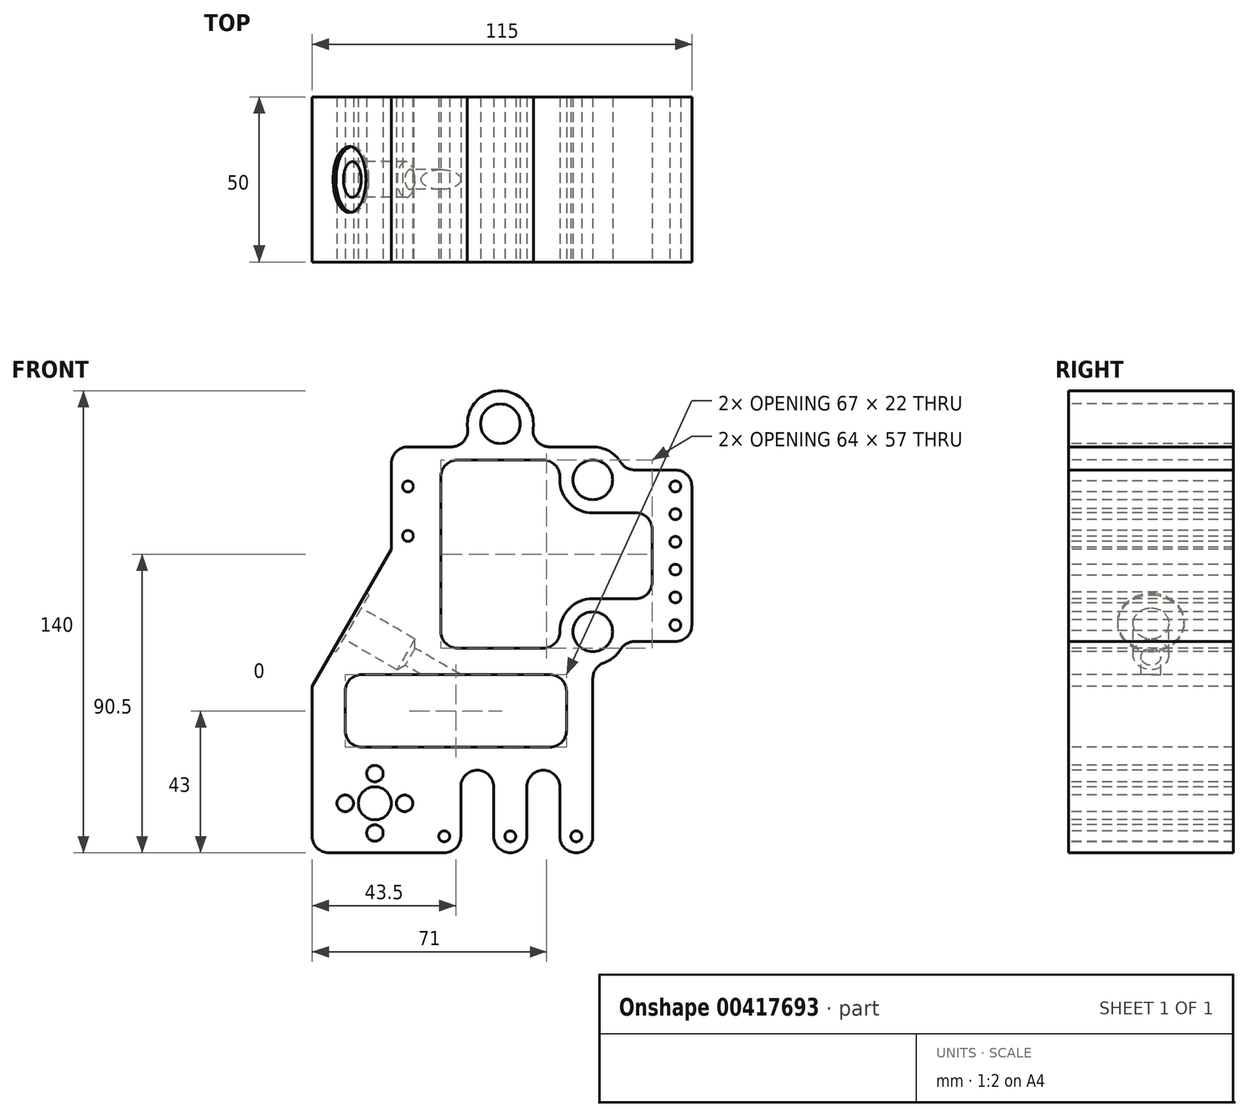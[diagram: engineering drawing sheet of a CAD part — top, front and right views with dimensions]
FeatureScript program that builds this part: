
annotation { "Feature Type Name" : "Feature", "Feature Type Description" : "" }
export const myFeature = defineFeature(function(context is Context, id is Id, definition is map)
    precondition{}
    {
        {
            var Q0;
            Q0=qCreatedBy(makeId("Front.planeOp"),FACE);
            var sketch = newSketch(context, id + "F0", { "sketchPlane" : qUnion([Q0])});
            skCircle(sketch, "E0", {"center": v(0, 50) * mm, "radius": 6 * mm});
            skCircle(sketch, "E1", {"center": v(28, 33) * mm, "radius": 6 * mm});
            skCircle(sketch, "E2", {"center": v(28, -13) * mm, "radius": 6 * mm});
            skLineSegment(sketch, "E3", {"start": v(0, 60.48) * mm, "end": v(0, 39.82) * mm, "construction": true});
            skLineSegment(sketch, "E4", {"start": v(-57, 50) * mm, "end": v(58, 50) * mm, "construction": true});
            skLineSegment(sketch, "E5", {"start": v(15.65, 33) * mm, "end": v(59.52, 33) * mm, "construction": true});
            skLineSegment(sketch, "E6", {"start": v(28, 45.63) * mm, "end": v(28, -22.58) * mm, "construction": true});
            skLineSegment(sketch, "E7", {"start": v(14.55, -13) * mm, "end": v(60.8, -13) * mm, "construction": true});
            skCircle(sketch, "E8", {"center": v(-28, 31) * mm, "radius": 2 * mm, "construction": true});
            skCircle(sketch, "E9", {"center": v(53, 31) * mm, "radius": 2 * mm, "construction": true});
            skCircle(sketch, "E10", {"center": v(23, -75) * mm, "radius": 2 * mm, "construction": true});
            skCircle(sketch, "E11", {"center": v(-38, -65) * mm, "radius": 5 * mm});
            skCircle(sketch, "E12", {"center": v(-38, -56) * mm, "radius": 3 * mm, "construction": true});
            skCircle(sketch, "E13.0.1.0", {"center": v(53, 22.6) * mm, "radius": 2 * mm, "construction": true});
            skCircle(sketch, "E13.0.2.0", {"center": v(53, 14.2) * mm, "radius": 2 * mm, "construction": true});
            skCircle(sketch, "E13.0.3.0", {"center": v(53, 5.8) * mm, "radius": 2 * mm, "construction": true});
            skCircle(sketch, "E13.0.4.0", {"center": v(53, -2.6) * mm, "radius": 2 * mm, "construction": true});
            skCircle(sketch, "E13.0.5.0", {"center": v(53, -11) * mm, "radius": 2 * mm, "construction": true});
            skLineSegment(sketch, "E13.direction1", {"start": v(53, 31) * mm, "end": v(78.37, 31) * mm, "construction": true});
            skLineSegment(sketch, "E13.direction2", {"start": v(53, 31) * mm, "end": v(53, 22.6) * mm, "construction": true});
            skCircle(sketch, "E14.0.1.0", {"center": v(-28, 16) * mm, "radius": 2 * mm, "construction": true});
            skLineSegment(sketch, "E14.direction1", {"start": v(-28, 31) * mm, "end": v(-13.33, 31) * mm, "construction": true});
            skLineSegment(sketch, "E14.direction2", {"start": v(-28, 31) * mm, "end": v(-28, 16) * mm, "construction": true});
            skCircle(sketch, "E15.1.0.0", {"center": v(3, -75) * mm, "radius": 2 * mm, "construction": true});
            skCircle(sketch, "E15.2.0.0", {"center": v(-17, -75) * mm, "radius": 2 * mm, "construction": true});
            skLineSegment(sketch, "E15.direction1", {"start": v(23, -75) * mm, "end": v(3, -75) * mm, "construction": true});
            skCircle(sketch, "E16.0", {"center": v(-38, -65) * mm, "radius": 9 * mm, "construction": true});
            skCircle(sketch, "E17.1.0", {"center": v(-47, -65) * mm, "radius": 3 * mm, "construction": true});
            skCircle(sketch, "E17.2.0", {"center": v(-38, -74) * mm, "radius": 3 * mm, "construction": true});
            skCircle(sketch, "E17.3.0", {"center": v(-29, -65) * mm, "radius": 3 * mm, "construction": true});
            skLineSegment(sketch, "E18", {"start": v(-57, 50) * mm, "end": v(-57, -80) * mm, "construction": true});
            skLineSegment(sketch, "E19", {"start": v(58, 50) * mm, "end": v(58, -80) * mm, "construction": true});
            skLineSegment(sketch, "E20", {"start": v(58, -80) * mm, "end": v(-57, -80) * mm, "construction": true});
            skSolve(sketch);
        }
        {
            var Q0;
            Q0=qCreatedBy(makeId("Front.planeOp"),FACE);
            var sketch = newSketch(context, id + "F1", { "sketchPlane" : qUnion([Q0])});
            skCircle(sketch, "E21.0", {"center": v(3, -75) * mm, "radius": 5 * mm});
            skLineSegment(sketch, "E22", {"start": v(53, 36) * mm, "end": v(40.69, 36) * mm});
            skArc(sketch, "E23", {"start": v(36.46, 38.33) * mm, "mid": v(38.27, 36.62) * mm, "end": v(40.69, 36) * mm});
            skLineSegment(sketch, "E24", {"start": v(58, 31) * mm, "end": v(58, -11) * mm});
            skLineSegment(sketch, "E25", {"start": v(53, -16) * mm, "end": v(40.69, -16) * mm});
            skArc(sketch, "E26", {"start": v(40.69, -16) * mm, "mid": v(38.27, -16.62) * mm, "end": v(36.46, -18.33) * mm});
            skLineSegment(sketch, "E27", {"start": v(28, -27.14) * mm, "end": v(28, -75) * mm});
            skArc(sketch, "E28", {"start": v(31.33, -22.43) * mm, "mid": v(28.92, -24.26) * mm, "end": v(28, -27.14) * mm});
            skLineSegment(sketch, "E29", {"start": v(18, -75) * mm, "end": v(18, -60) * mm});
            skArc(sketch, "E30", {"start": v(18, -60) * mm, "mid": v(13, -55) * mm, "end": v(8, -60) * mm});
            skLineSegment(sketch, "E31", {"start": v(8, -60) * mm, "end": v(8, -75) * mm});
            skLineSegment(sketch, "E32.1.0.0", {"start": v(-12, -60) * mm, "end": v(-12, -75) * mm});
            skArc(sketch, "E32.1.0.1", {"start": v(-2, -60) * mm, "mid": v(-7, -55) * mm, "end": v(-12, -60) * mm});
            skLineSegment(sketch, "E32.1.0.2", {"start": v(-2, -75) * mm, "end": v(-2, -60) * mm});
            skLineSegment(sketch, "E32.direction1", {"start": v(8, -75) * mm, "end": v(-12, -75) * mm, "construction": true});
            skLineSegment(sketch, "E33", {"start": v(-17, -80) * mm, "end": v(-52, -80) * mm});
            skArc(sketch, "E34", {"start": v(-57, -75) * mm, "mid": v(-55.54, -78.54) * mm, "end": v(-52, -80) * mm});
            skLineSegment(sketch, "E35", {"start": v(-57, -75) * mm, "end": v(-57, -29.57) * mm});
            skLineSegment(sketch, "E36", {"start": v(-57, -29.57) * mm, "end": v(-33, 12) * mm});
            skLineSegment(sketch, "E37", {"start": v(-33, 12) * mm, "end": v(-33, 38) * mm});
            skArc(sketch, "E38", {"start": v(-28, 43) * mm, "mid": v(-31.54, 41.54) * mm, "end": v(-33, 38) * mm});
            skLineSegment(sketch, "E39", {"start": v(-28, 43) * mm, "end": v(-14.87, 43) * mm});
            skArc(sketch, "E40", {"start": v(-14.87, 43) * mm, "mid": v(-11.1, 44.7) * mm, "end": v(-9.91, 48.67) * mm});
            skLineSegment(sketch, "E41", {"start": v(28, 43) * mm, "end": v(14.87, 43) * mm});
            skArc(sketch, "E42", {"start": v(9.91, 48.67) * mm, "mid": v(11.1, 44.7) * mm, "end": v(14.87, 43) * mm});
            skArc(sketch, "E43", {"start": v(9.91, 48.67) * mm, "mid": v(0, 60) * mm, "end": v(-9.91, 48.67) * mm});
            skArc(sketch, "E44", {"start": v(-9.91, 48.67) * mm, "mid": v(0, 40) * mm, "end": v(9.91, 48.67) * mm, "construction": true});
            skArc(sketch, "E45", {"start": v(28, 43) * mm, "mid": v(23.17, 24.24) * mm, "end": v(36.46, 38.33) * mm, "construction": true});
            skArc(sketch, "E46", {"start": v(36.46, 38.33) * mm, "mid": v(32.83, 41.76) * mm, "end": v(28, 43) * mm});
            skArc(sketch, "E47", {"start": v(53, 36) * mm, "mid": v(49.46, 27.46) * mm, "end": v(58, 31) * mm, "construction": true});
            skArc(sketch, "E48", {"start": v(58, 31) * mm, "mid": v(56.54, 34.54) * mm, "end": v(53, 36) * mm});
            skArc(sketch, "E49", {"start": v(58, -11) * mm, "mid": v(49.46, -7.46) * mm, "end": v(53, -16) * mm, "construction": true});
            skArc(sketch, "E50", {"start": v(53, -16) * mm, "mid": v(56.54, -14.54) * mm, "end": v(58, -11) * mm});
            skArc(sketch, "E51", {"start": v(36.46, -18.33) * mm, "mid": v(21.76, -5.19) * mm, "end": v(31.33, -22.43) * mm, "construction": true});
            skArc(sketch, "E52", {"start": v(31.33, -22.43) * mm, "mid": v(34.24, -20.81) * mm, "end": v(36.46, -18.33) * mm});
            skArc(sketch, "E53", {"start": v(28, -75) * mm, "mid": v(23, -70) * mm, "end": v(18, -75) * mm, "construction": true});
            skArc(sketch, "E54", {"start": v(18, -75) * mm, "mid": v(23, -80) * mm, "end": v(28, -75) * mm});
            skArc(sketch, "E55", {"start": v(-12, -75) * mm, "mid": v(-20.54, -71.46) * mm, "end": v(-17, -80) * mm, "construction": true});
            skArc(sketch, "E56", {"start": v(-17, -80) * mm, "mid": v(-13.46, -78.54) * mm, "end": v(-12, -75) * mm});
            skLineSegment(sketch, "E57", {"start": v(-18, 34) * mm, "end": v(-18, -13) * mm});
            skArc(sketch, "E58", {"start": v(-18, -13) * mm, "mid": v(-16.54, -16.54) * mm, "end": v(-13, -18) * mm});
            skLineSegment(sketch, "E59", {"start": v(-13, -18) * mm, "end": v(13, -18) * mm});
            skArc(sketch, "E60", {"start": v(13, -18) * mm, "mid": v(16.54, -16.54) * mm, "end": v(18, -13) * mm});
            skArc(sketch, "E61", {"start": v(-13, 39) * mm, "mid": v(-16.54, 37.54) * mm, "end": v(-18, 34) * mm});
            skLineSegment(sketch, "E62", {"start": v(-13, 39) * mm, "end": v(13, 39) * mm});
            skArc(sketch, "E63", {"start": v(18, 33) * mm, "mid": v(20.93, 25.93) * mm, "end": v(28, 23) * mm});
            skLineSegment(sketch, "E64", {"start": v(28, 23) * mm, "end": v(41, 23) * mm});
            skArc(sketch, "E65", {"start": v(46, 18) * mm, "mid": v(44.54, 21.54) * mm, "end": v(41, 23) * mm});
            skLineSegment(sketch, "E66", {"start": v(46, 18) * mm, "end": v(46, 2) * mm});
            skArc(sketch, "E67", {"start": v(41, -3) * mm, "mid": v(44.54, -1.54) * mm, "end": v(46, 2) * mm});
            skLineSegment(sketch, "E68", {"start": v(41, -3) * mm, "end": v(28, -3) * mm});
            skLineSegment(sketch, "E69", {"start": v(18, 33) * mm, "end": v(18, 34) * mm});
            skArc(sketch, "E70", {"start": v(18, 34) * mm, "mid": v(16.54, 37.54) * mm, "end": v(13, 39) * mm});
            skLineSegment(sketch, "E71", {"start": v(18, -13) * mm, "end": v(18, -13) * mm});
            skArc(sketch, "E72", {"start": v(28, -3) * mm, "mid": v(20.93, -5.93) * mm, "end": v(18, -13) * mm});
            skLineSegment(sketch, "E73.bottom", {"start": v(-42, -26) * mm, "end": v(15, -26) * mm});
            skLineSegment(sketch, "E73.top", {"start": v(-42, -48) * mm, "end": v(15, -48) * mm});
            skLineSegment(sketch, "E73.left", {"start": v(-47, -31) * mm, "end": v(-47, -43) * mm});
            skLineSegment(sketch, "E73.right", {"start": v(20, -31) * mm, "end": v(20, -43) * mm});
            skPoint(sketch, "E74.visualSharp", {"position": v(-47, -26) * mm});
            skArc(sketch, "E74.filletArc", {"start": v(-42, -26) * mm, "mid": v(-45.54, -27.46) * mm, "end": v(-47, -31) * mm});
            skPoint(sketch, "E75.visualSharp", {"position": v(-47, -48) * mm});
            skArc(sketch, "E75.filletArc", {"start": v(-47, -43) * mm, "mid": v(-45.54, -46.54) * mm, "end": v(-42, -48) * mm});
            skPoint(sketch, "E76.visualSharp", {"position": v(20, -26) * mm});
            skArc(sketch, "E76.filletArc", {"start": v(20, -31) * mm, "mid": v(18.54, -27.46) * mm, "end": v(15, -26) * mm});
            skPoint(sketch, "E77.visualSharp", {"position": v(20, -48) * mm});
            skArc(sketch, "E77.filletArc", {"start": v(15, -48) * mm, "mid": v(18.54, -46.54) * mm, "end": v(20, -43) * mm});
            skSolve(sketch);
        }
        {
            var Q0;
            Q0 = qSketchRegion(id + "F1", true);
            extrude(context, id + "F2", {"entities" : qUnion([Q0]), "oppositeDirection" : true, "depth" : 50 * mm});
        }
        {
            var Q0;
            Q0 = qSketchRegion(id + "F0", true);
            extrude(context, id + "F3", {"entities" : qUnion([Q0]), "operationType" : NewBodyOperationType.REMOVE, "endBound" : BoundingType.THROUGH_ALL, "oppositeDirection" : true, "depth" : 25 * mm});
        }
        {
            var Q0;
            Q0=sQuery(id+"F0.wireOp",VERTEX,"E13.direction2.start");
            var Q1;
            Q1=sQuery(id+"F0.wireOp",VERTEX,"E13.0.1.0.center");
            var Q2;
            Q2=sQuery(id+"F0.wireOp",VERTEX,"E13.0.2.0.center");
            var Q3;
            Q3=sQuery(id+"F0.wireOp",VERTEX,"E13.0.3.0.center");
            var Q4;
            Q4=sQuery(id+"F0.wireOp",VERTEX,"E13.0.4.0.center");
            var Q5;
            Q5=sQuery(id+"F0.wireOp",VERTEX,"E13.0.5.0.center");
            var Q6;
            Q6=sQuery(id+"F0.wireOp",VERTEX,"E14.direction2.end");
            var Q7;
            Q7=sQuery(id+"F0.wireOp",VERTEX,"E14.direction2.start");
            var Q8;
            Q8=sQuery(id+"F0.wireOp",VERTEX,"E15.2.0.0.center");
            var Q9;
            Q9=sQuery(id+"F0.wireOp",VERTEX,"E15.1.0.0.center");
            var Q10;
            Q10=sQuery(id+"F0.wireOp",VERTEX,"E15.direction1.start");
            var Q11;
            Q11=makeQuery(id+"F2.opExtrude","SWEPT_BODY",BODY,{"disambiguationData":[OSD([sQuery(id+"F1.wireOp",EDGE,"E21.0"),sQuery(id+"F1.wireOp",EDGE,"E22"),sQuery(id+"F1.wireOp",EDGE,"E23"),sQuery(id+"F1.wireOp",EDGE,"E24"),sQuery(id+"F1.wireOp",EDGE,"E25"),sQuery(id+"F1.wireOp",EDGE,"E26"),sQuery(id+"F1.wireOp",EDGE,"E27"),sQuery(id+"F1.wireOp",EDGE,"E28"),sQuery(id+"F1.wireOp",EDGE,"E29"),sQuery(id+"F1.wireOp",EDGE,"E30"),sQuery(id+"F1.wireOp",EDGE,"E31"),sQuery(id+"F1.wireOp",EDGE,"E32.1.0.0"),sQuery(id+"F1.wireOp",EDGE,"E32.1.0.1"),sQuery(id+"F1.wireOp",EDGE,"E32.1.0.2"),sQuery(id+"F1.wireOp",EDGE,"E33"),sQuery(id+"F1.wireOp",EDGE,"E34"),sQuery(id+"F1.wireOp",EDGE,"E35"),sQuery(id+"F1.wireOp",EDGE,"E36"),sQuery(id+"F1.wireOp",EDGE,"E37"),sQuery(id+"F1.wireOp",EDGE,"E38"),sQuery(id+"F1.wireOp",EDGE,"E39"),sQuery(id+"F1.wireOp",EDGE,"E40"),sQuery(id+"F1.wireOp",EDGE,"E41"),sQuery(id+"F1.wireOp",EDGE,"E42"),sQuery(id+"F1.wireOp",EDGE,"E43"),sQuery(id+"F1.wireOp",EDGE,"E46"),sQuery(id+"F1.wireOp",EDGE,"E48"),sQuery(id+"F1.wireOp",EDGE,"E50"),sQuery(id+"F1.wireOp",EDGE,"E52"),sQuery(id+"F1.wireOp",EDGE,"E54"),sQuery(id+"F1.wireOp",EDGE,"E56"),sQuery(id+"F1.wireOp",EDGE,"E57"),sQuery(id+"F1.wireOp",EDGE,"E58"),sQuery(id+"F1.wireOp",EDGE,"E59"),sQuery(id+"F1.wireOp",EDGE,"E60"),sQuery(id+"F1.wireOp",EDGE,"E61"),sQuery(id+"F1.wireOp",EDGE,"E62"),sQuery(id+"F1.wireOp",EDGE,"E63"),sQuery(id+"F1.wireOp",EDGE,"E64"),sQuery(id+"F1.wireOp",EDGE,"E65"),sQuery(id+"F1.wireOp",EDGE,"E66"),sQuery(id+"F1.wireOp",EDGE,"E67"),sQuery(id+"F1.wireOp",EDGE,"E68"),sQuery(id+"F1.wireOp",EDGE,"E69"),sQuery(id+"F1.wireOp",EDGE,"E70"),sQuery(id+"F1.wireOp",EDGE,"E72"),sQuery(id+"F1.wireOp",EDGE,"E73.bottom"),sQuery(id+"F1.wireOp",EDGE,"E73.top"),sQuery(id+"F1.wireOp",EDGE,"E73.left"),sQuery(id+"F1.wireOp",EDGE,"E73.right"),sQuery(id+"F1.wireOp",EDGE,"E74.filletArc"),sQuery(id+"F1.wireOp",EDGE,"E75.filletArc"),sQuery(id+"F1.wireOp",EDGE,"E76.filletArc"),sQuery(id+"F1.wireOp",EDGE,"E77.filletArc")])]});
            hole(context, id + "F4", {"style" : HoleStyle.SIMPLE, "endStyle" : HoleEndStyle.THROUGH, "standardTappedOrClearance" : lookupTablePath({ "standard" : "ISO", "engagement" : "75%", "pitch" : "0.7 mm", "size" : "M4", "type" : "Tapped" }), "standardBlindInLast" : lookupTablePath({ "standard" : "ISO", "engagement" : "75%", "pitch" : "0.7 mm", "size" : "M4", "type" : "Tapped" }), "holeDiameter" : 3.3 * mm, "showTappedDepth" : true, "isTappedThrough" : true, "tappedDepth" : 12 * mm, "tapClearance" : 3, "locations" : qUnion([Q0, Q1, Q2, Q3, Q4, Q5, Q6, Q7, Q8, Q9, Q10]), "scope" : qUnion([Q11]), "majorDiameter" : 4 * mm});
        }
        {
            var Q0;
            Q0=sQuery(id+"F0.wireOp",VERTEX,"E17.1.0.center");
            var Q1;
            Q1=sQuery(id+"F0.wireOp",VERTEX,"E12.center");
            var Q2;
            Q2=sQuery(id+"F0.wireOp",VERTEX,"E17.3.0.center");
            var Q3;
            Q3=sQuery(id+"F0.wireOp",VERTEX,"E17.2.0.center");
            var Q4;
            Q4=makeQuery(id+"F2.opExtrude","SWEPT_BODY",BODY,{"disambiguationData":[OSD([sQuery(id+"F1.wireOp",EDGE,"E21.0"),sQuery(id+"F1.wireOp",EDGE,"E22"),sQuery(id+"F1.wireOp",EDGE,"E23"),sQuery(id+"F1.wireOp",EDGE,"E24"),sQuery(id+"F1.wireOp",EDGE,"E25"),sQuery(id+"F1.wireOp",EDGE,"E26"),sQuery(id+"F1.wireOp",EDGE,"E27"),sQuery(id+"F1.wireOp",EDGE,"E28"),sQuery(id+"F1.wireOp",EDGE,"E29"),sQuery(id+"F1.wireOp",EDGE,"E30"),sQuery(id+"F1.wireOp",EDGE,"E31"),sQuery(id+"F1.wireOp",EDGE,"E32.1.0.0"),sQuery(id+"F1.wireOp",EDGE,"E32.1.0.1"),sQuery(id+"F1.wireOp",EDGE,"E32.1.0.2"),sQuery(id+"F1.wireOp",EDGE,"E33"),sQuery(id+"F1.wireOp",EDGE,"E34"),sQuery(id+"F1.wireOp",EDGE,"E35"),sQuery(id+"F1.wireOp",EDGE,"E36"),sQuery(id+"F1.wireOp",EDGE,"E37"),sQuery(id+"F1.wireOp",EDGE,"E38"),sQuery(id+"F1.wireOp",EDGE,"E39"),sQuery(id+"F1.wireOp",EDGE,"E40"),sQuery(id+"F1.wireOp",EDGE,"E41"),sQuery(id+"F1.wireOp",EDGE,"E42"),sQuery(id+"F1.wireOp",EDGE,"E43"),sQuery(id+"F1.wireOp",EDGE,"E46"),sQuery(id+"F1.wireOp",EDGE,"E48"),sQuery(id+"F1.wireOp",EDGE,"E50"),sQuery(id+"F1.wireOp",EDGE,"E52"),sQuery(id+"F1.wireOp",EDGE,"E54"),sQuery(id+"F1.wireOp",EDGE,"E56"),sQuery(id+"F1.wireOp",EDGE,"E57"),sQuery(id+"F1.wireOp",EDGE,"E58"),sQuery(id+"F1.wireOp",EDGE,"E59"),sQuery(id+"F1.wireOp",EDGE,"E60"),sQuery(id+"F1.wireOp",EDGE,"E61"),sQuery(id+"F1.wireOp",EDGE,"E62"),sQuery(id+"F1.wireOp",EDGE,"E63"),sQuery(id+"F1.wireOp",EDGE,"E64"),sQuery(id+"F1.wireOp",EDGE,"E65"),sQuery(id+"F1.wireOp",EDGE,"E66"),sQuery(id+"F1.wireOp",EDGE,"E67"),sQuery(id+"F1.wireOp",EDGE,"E68"),sQuery(id+"F1.wireOp",EDGE,"E69"),sQuery(id+"F1.wireOp",EDGE,"E70"),sQuery(id+"F1.wireOp",EDGE,"E72"),sQuery(id+"F1.wireOp",EDGE,"E73.bottom"),sQuery(id+"F1.wireOp",EDGE,"E73.top"),sQuery(id+"F1.wireOp",EDGE,"E73.left"),sQuery(id+"F1.wireOp",EDGE,"E73.right"),sQuery(id+"F1.wireOp",EDGE,"E74.filletArc"),sQuery(id+"F1.wireOp",EDGE,"E75.filletArc"),sQuery(id+"F1.wireOp",EDGE,"E76.filletArc"),sQuery(id+"F1.wireOp",EDGE,"E77.filletArc")])]});
            hole(context, id + "F5", {"style" : HoleStyle.SIMPLE, "endStyle" : HoleEndStyle.THROUGH, "standardTappedOrClearance" : lookupTablePath({ "standard" : "ISO", "engagement" : "75%", "pitch" : "1 mm", "size" : "M6", "type" : "Tapped" }), "standardBlindInLast" : lookupTablePath({ "standard" : "ISO", "engagement" : "75%", "pitch" : "1 mm", "size" : "M6", "type" : "Tapped" }), "holeDiameter" : 5 * mm, "showTappedDepth" : true, "isTappedThrough" : true, "tappedDepth" : 12 * mm, "tapClearance" : 3, "locations" : qUnion([Q0, Q1, Q2, Q3]), "scope" : qUnion([Q4]), "majorDiameter" : 6 * mm});
        }
        {
            var Q0;
            Q0=qCreatedBy(makeId("Front.planeOp"),FACE);
            var sketch = newSketch(context, id + "F6", { "sketchPlane" : qUnion([Q0])});
            skLineSegment(sketch, "E78", {"start": v(-55.95, -4.09) * mm, "end": v(-12.75, -29.03) * mm, "construction": true});
            skPoint(sketch, "E79", {"position": v(-18, -26) * mm});
            skSolve(sketch);
        }
        {
            var Q0;
            Q0=makeQuery(id+"F2.opExtrude","SWEPT_FACE",FACE,{"disambiguationData":[OSD([sQuery(id+"F1.wireOp",EDGE,"E36")])]});
            var sketch = newSketch(context, id + "F7", { "sketchPlane" : qUnion([Q0])});
            skLineSegment(sketch, "E80", {"start": v(-25, -6.1) * mm, "end": v(-25, -54.1) * mm, "construction": true});
            skCircle(sketch, "E81", {"center": v(-25, -31.52) * mm, "radius": 10 * mm});
            skPoint(sketch, "E82.0", {"position": v(0, -31.52) * mm});
            skSolve(sketch);
        }
        {
            var Q0;
            Q0 = qSketchRegion(id + "F7", true);
            extrude(context, id + "F8", {"entities" : qUnion([Q0]), "operationType" : NewBodyOperationType.REMOVE, "oppositeDirection" : true, "depth" : 1 * mm});
        }
        {
            var Q0;
            Q0=sQuery(id+"F7.wireOp",VERTEX,"E81.center");
            var Q1;
            Q1=makeQuery(id+"F2.opExtrude","SWEPT_BODY",BODY,{"disambiguationData":[OSD([sQuery(id+"F1.wireOp",EDGE,"E21.0"),sQuery(id+"F1.wireOp",EDGE,"E22"),sQuery(id+"F1.wireOp",EDGE,"E23"),sQuery(id+"F1.wireOp",EDGE,"E24"),sQuery(id+"F1.wireOp",EDGE,"E25"),sQuery(id+"F1.wireOp",EDGE,"E26"),sQuery(id+"F1.wireOp",EDGE,"E27"),sQuery(id+"F1.wireOp",EDGE,"E28"),sQuery(id+"F1.wireOp",EDGE,"E29"),sQuery(id+"F1.wireOp",EDGE,"E30"),sQuery(id+"F1.wireOp",EDGE,"E31"),sQuery(id+"F1.wireOp",EDGE,"E32.1.0.0"),sQuery(id+"F1.wireOp",EDGE,"E32.1.0.1"),sQuery(id+"F1.wireOp",EDGE,"E32.1.0.2"),sQuery(id+"F1.wireOp",EDGE,"E33"),sQuery(id+"F1.wireOp",EDGE,"E34"),sQuery(id+"F1.wireOp",EDGE,"E35"),sQuery(id+"F1.wireOp",EDGE,"E36"),sQuery(id+"F1.wireOp",EDGE,"E37"),sQuery(id+"F1.wireOp",EDGE,"E38"),sQuery(id+"F1.wireOp",EDGE,"E39"),sQuery(id+"F1.wireOp",EDGE,"E40"),sQuery(id+"F1.wireOp",EDGE,"E41"),sQuery(id+"F1.wireOp",EDGE,"E42"),sQuery(id+"F1.wireOp",EDGE,"E43"),sQuery(id+"F1.wireOp",EDGE,"E46"),sQuery(id+"F1.wireOp",EDGE,"E48"),sQuery(id+"F1.wireOp",EDGE,"E50"),sQuery(id+"F1.wireOp",EDGE,"E52"),sQuery(id+"F1.wireOp",EDGE,"E54"),sQuery(id+"F1.wireOp",EDGE,"E56"),sQuery(id+"F1.wireOp",EDGE,"E57"),sQuery(id+"F1.wireOp",EDGE,"E58"),sQuery(id+"F1.wireOp",EDGE,"E59"),sQuery(id+"F1.wireOp",EDGE,"E60"),sQuery(id+"F1.wireOp",EDGE,"E61"),sQuery(id+"F1.wireOp",EDGE,"E62"),sQuery(id+"F1.wireOp",EDGE,"E63"),sQuery(id+"F1.wireOp",EDGE,"E64"),sQuery(id+"F1.wireOp",EDGE,"E65"),sQuery(id+"F1.wireOp",EDGE,"E66"),sQuery(id+"F1.wireOp",EDGE,"E67"),sQuery(id+"F1.wireOp",EDGE,"E68"),sQuery(id+"F1.wireOp",EDGE,"E69"),sQuery(id+"F1.wireOp",EDGE,"E70"),sQuery(id+"F1.wireOp",EDGE,"E72"),sQuery(id+"F1.wireOp",EDGE,"E73.bottom"),sQuery(id+"F1.wireOp",EDGE,"E73.top"),sQuery(id+"F1.wireOp",EDGE,"E73.left"),sQuery(id+"F1.wireOp",EDGE,"E73.right"),sQuery(id+"F1.wireOp",EDGE,"E74.filletArc"),sQuery(id+"F1.wireOp",EDGE,"E75.filletArc"),sQuery(id+"F1.wireOp",EDGE,"E76.filletArc"),sQuery(id+"F1.wireOp",EDGE,"E77.filletArc")])]});
            hole(context, id + "F9", {"style" : HoleStyle.SIMPLE, "endStyle" : HoleEndStyle.BLIND, "standardTappedOrClearance" : lookupTablePath({ "standard" : "ISO", "engagement" : "75%", "pitch" : "1.25 mm", "size" : "M12", "type" : "Tapped" }), "standardBlindInLast" : lookupTablePath({ "standard" : "ISO", "engagement" : "75%", "pitch" : "1.25 mm", "size" : "M12", "type" : "Tapped" }), "holeDiameter" : 10.8 * mm, "showTappedDepth" : true, "holeDepth" : 18.75 * mm, "tappedDepth" : 15 * mm, "tapClearance" : 3, "locations" : qUnion([Q0]), "scope" : qUnion([Q1]), "majorDiameter" : 12 * mm});
        }
        {
            var Q0;
            Q0=sQuery(id+"F7.wireOp",VERTEX,"E81.center");
            var Q1;
            Q1=makeQuery(id+"F2.opExtrude","SWEPT_BODY",BODY,{"disambiguationData":[OSD([sQuery(id+"F1.wireOp",EDGE,"E21.0"),sQuery(id+"F1.wireOp",EDGE,"E22"),sQuery(id+"F1.wireOp",EDGE,"E23"),sQuery(id+"F1.wireOp",EDGE,"E24"),sQuery(id+"F1.wireOp",EDGE,"E25"),sQuery(id+"F1.wireOp",EDGE,"E26"),sQuery(id+"F1.wireOp",EDGE,"E27"),sQuery(id+"F1.wireOp",EDGE,"E28"),sQuery(id+"F1.wireOp",EDGE,"E29"),sQuery(id+"F1.wireOp",EDGE,"E30"),sQuery(id+"F1.wireOp",EDGE,"E31"),sQuery(id+"F1.wireOp",EDGE,"E32.1.0.0"),sQuery(id+"F1.wireOp",EDGE,"E32.1.0.1"),sQuery(id+"F1.wireOp",EDGE,"E32.1.0.2"),sQuery(id+"F1.wireOp",EDGE,"E33"),sQuery(id+"F1.wireOp",EDGE,"E34"),sQuery(id+"F1.wireOp",EDGE,"E35"),sQuery(id+"F1.wireOp",EDGE,"E36"),sQuery(id+"F1.wireOp",EDGE,"E37"),sQuery(id+"F1.wireOp",EDGE,"E38"),sQuery(id+"F1.wireOp",EDGE,"E39"),sQuery(id+"F1.wireOp",EDGE,"E40"),sQuery(id+"F1.wireOp",EDGE,"E41"),sQuery(id+"F1.wireOp",EDGE,"E42"),sQuery(id+"F1.wireOp",EDGE,"E43"),sQuery(id+"F1.wireOp",EDGE,"E46"),sQuery(id+"F1.wireOp",EDGE,"E48"),sQuery(id+"F1.wireOp",EDGE,"E50"),sQuery(id+"F1.wireOp",EDGE,"E52"),sQuery(id+"F1.wireOp",EDGE,"E54"),sQuery(id+"F1.wireOp",EDGE,"E56"),sQuery(id+"F1.wireOp",EDGE,"E57"),sQuery(id+"F1.wireOp",EDGE,"E58"),sQuery(id+"F1.wireOp",EDGE,"E59"),sQuery(id+"F1.wireOp",EDGE,"E60"),sQuery(id+"F1.wireOp",EDGE,"E61"),sQuery(id+"F1.wireOp",EDGE,"E62"),sQuery(id+"F1.wireOp",EDGE,"E63"),sQuery(id+"F1.wireOp",EDGE,"E64"),sQuery(id+"F1.wireOp",EDGE,"E65"),sQuery(id+"F1.wireOp",EDGE,"E66"),sQuery(id+"F1.wireOp",EDGE,"E67"),sQuery(id+"F1.wireOp",EDGE,"E68"),sQuery(id+"F1.wireOp",EDGE,"E69"),sQuery(id+"F1.wireOp",EDGE,"E70"),sQuery(id+"F1.wireOp",EDGE,"E72"),sQuery(id+"F1.wireOp",EDGE,"E73.bottom"),sQuery(id+"F1.wireOp",EDGE,"E73.top"),sQuery(id+"F1.wireOp",EDGE,"E73.left"),sQuery(id+"F1.wireOp",EDGE,"E73.right"),sQuery(id+"F1.wireOp",EDGE,"E74.filletArc"),sQuery(id+"F1.wireOp",EDGE,"E75.filletArc"),sQuery(id+"F1.wireOp",EDGE,"E76.filletArc"),sQuery(id+"F1.wireOp",EDGE,"E77.filletArc")])]});
            hole(context, id + "F10", {"style" : HoleStyle.SIMPLE, "endStyle" : HoleEndStyle.BLIND, "holeDiameter" : 6 * mm, "holeDepth" : 18.75 * mm, "tappedDepth" : 15 * mm, "tapClearance" : 3, "locations" : qUnion([Q0]), "scope" : qUnion([Q1])});
        }
    });
